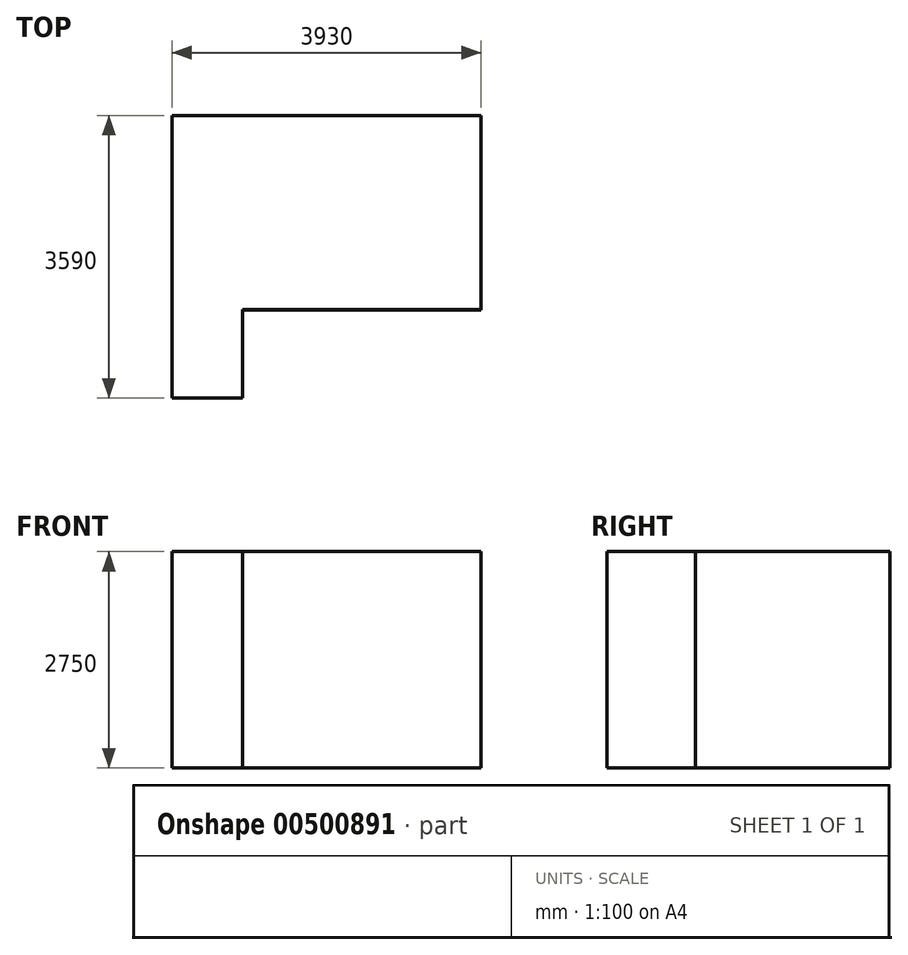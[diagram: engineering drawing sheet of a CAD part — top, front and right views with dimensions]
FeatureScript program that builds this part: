
annotation { "Feature Type Name" : "Feature", "Feature Type Description" : "" }
export const myFeature = defineFeature(function(context is Context, id is Id, definition is map)
    precondition{}
    {
        {
            var Q0;
            Q0=qCreatedBy(makeId("Top.planeOp"),FACE);
            var sketch = newSketch(context, id + "F0", { "sketchPlane" : qUnion([Q0])});
            skLineSegment(sketch, "E0.bottom", {"start": v(0, 0) * mm, "end": v(900, 0) * mm});
            skLineSegment(sketch, "E0.top", {"start": v(0, 3590) * mm, "end": v(3930, 3590) * mm});
            skLineSegment(sketch, "E0.left", {"start": v(0, 0) * mm, "end": v(0, 3590) * mm});
            skLineSegment(sketch, "E0.right", {"start": v(3930, 1120) * mm, "end": v(3930, 3590) * mm});
            skLineSegment(sketch, "E1.top", {"start": v(3930, 1120) * mm, "end": v(900, 1120) * mm});
            skLineSegment(sketch, "E1.right", {"start": v(900, 0) * mm, "end": v(900, 1120) * mm});
            skSolve(sketch);
        }
        {
            var Q0;
            Q0 = qSketchRegion(id + "F0", true);
            extrude(context, id + "F1", {"entities" : qUnion([Q0]), "depth" : 2750 * mm, "offsetDistance" : 25 * mm});
        }
        {
            var Q0;
            Q0=makeQuery(id+"F1.opExtrude","CAP_FACE",FACE,{"disambiguationData":[OSD([sQuery(id+"F0.wireOp",EDGE,"E0.bottom"),sQuery(id+"F0.wireOp",EDGE,"E0.top"),sQuery(id+"F0.wireOp",EDGE,"E0.left"),sQuery(id+"F0.wireOp",EDGE,"E0.right"),sQuery(id+"F0.wireOp",EDGE,"E1.top"),sQuery(id+"F0.wireOp",EDGE,"E1.right")])],"isStart":false});
            shell(context, id + "F2", {"entities" : qUnion([Q0]), "thickness" : 2.5 * mm});
        }
    });
